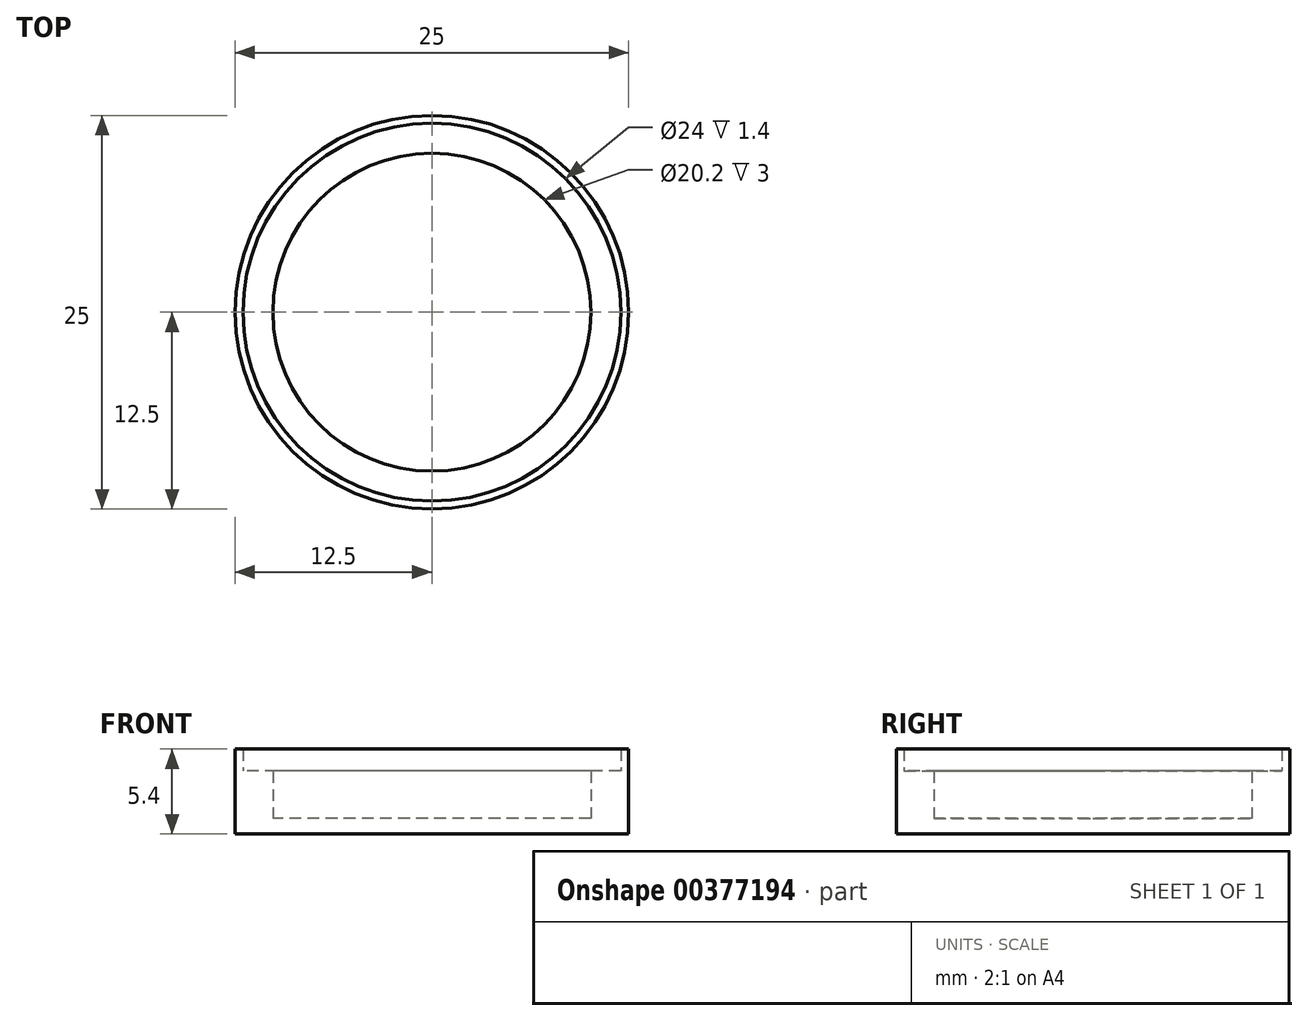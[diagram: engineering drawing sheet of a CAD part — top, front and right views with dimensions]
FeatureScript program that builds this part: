
annotation { "Feature Type Name" : "Feature", "Feature Type Description" : "" }
export const myFeature = defineFeature(function(context is Context, id is Id, definition is map)
    precondition{}
    {
        {
            var Q0;
            Q0=qCreatedBy(makeId("Top.planeOp"),FACE);
            var sketch = newSketch(context, id + "F0", { "sketchPlane" : qUnion([Q0])});
            skCircle(sketch, "E0", {"center": v(0, 0) * mm, "radius": 12.5 * mm});
            skCircle(sketch, "E1", {"center": v(0, 0) * mm, "radius": 12 * mm});
            skSolve(sketch);
        }
        {
            var Q0;
            Q0=makeQuery(id+"F0.imprint","IMPRINT",FACE,{"disambiguationData":[TD([[makeQuery(id+"F0.imprint","IMPRINT",EDGE,{"derivedFrom":sQuery(id+"F0.wireOp",EDGE,"E0")}),1.0]])]});
            extrude(context, id + "F1", {"entities" : qUnion([Q0]), "depth" : 5.4 * mm});
        }
        {
            var Q0;
            Q0=qCreatedBy(makeId("Top.planeOp"),FACE);
            var sketch = newSketch(context, id + "F2", { "sketchPlane" : qUnion([Q0])});
            skCircle(sketch, "E2", {"center": v(0, 0) * mm, "radius": 12.5 * mm});
            skSolve(sketch);
        }
        {
            var Q0;
            Q0=makeQuery(id+"F2.imprint","IMPRINT",FACE,{"disambiguationData":[TD([[makeQuery(id+"F2.imprint","IMPRINT",EDGE,{"derivedFrom":sQuery(id+"F2.wireOp",EDGE,"E2")}),1.0]])]});
            extrude(context, id + "F3", {"entities" : qUnion([Q0]), "operationType" : NewBodyOperationType.ADD, "depth" : 1 * mm});
        }
        {
            var Q0;
            Q0=qCreatedBy(makeId("Top.planeOp"),FACE);
            var sketch = newSketch(context, id + "F4", { "sketchPlane" : qUnion([Q0])});
            skCircle(sketch, "E3", {"center": v(0, 0) * mm, "radius": 12.5 * mm});
            skCircle(sketch, "E4", {"center": v(0, 0) * mm, "radius": 10.1 * mm});
            skSolve(sketch);
        }
        {
            var Q0;
            Q0=makeQuery(id+"F4.imprint","IMPRINT",FACE,{"disambiguationData":[TD([[makeQuery(id+"F4.imprint","IMPRINT",EDGE,{"derivedFrom":sQuery(id+"F4.wireOp",EDGE,"E3")}),1.0]])]});
            extrude(context, id + "F5", {"entities" : qUnion([Q0]), "operationType" : NewBodyOperationType.ADD, "depth" : 4 * mm});
        }
    });
